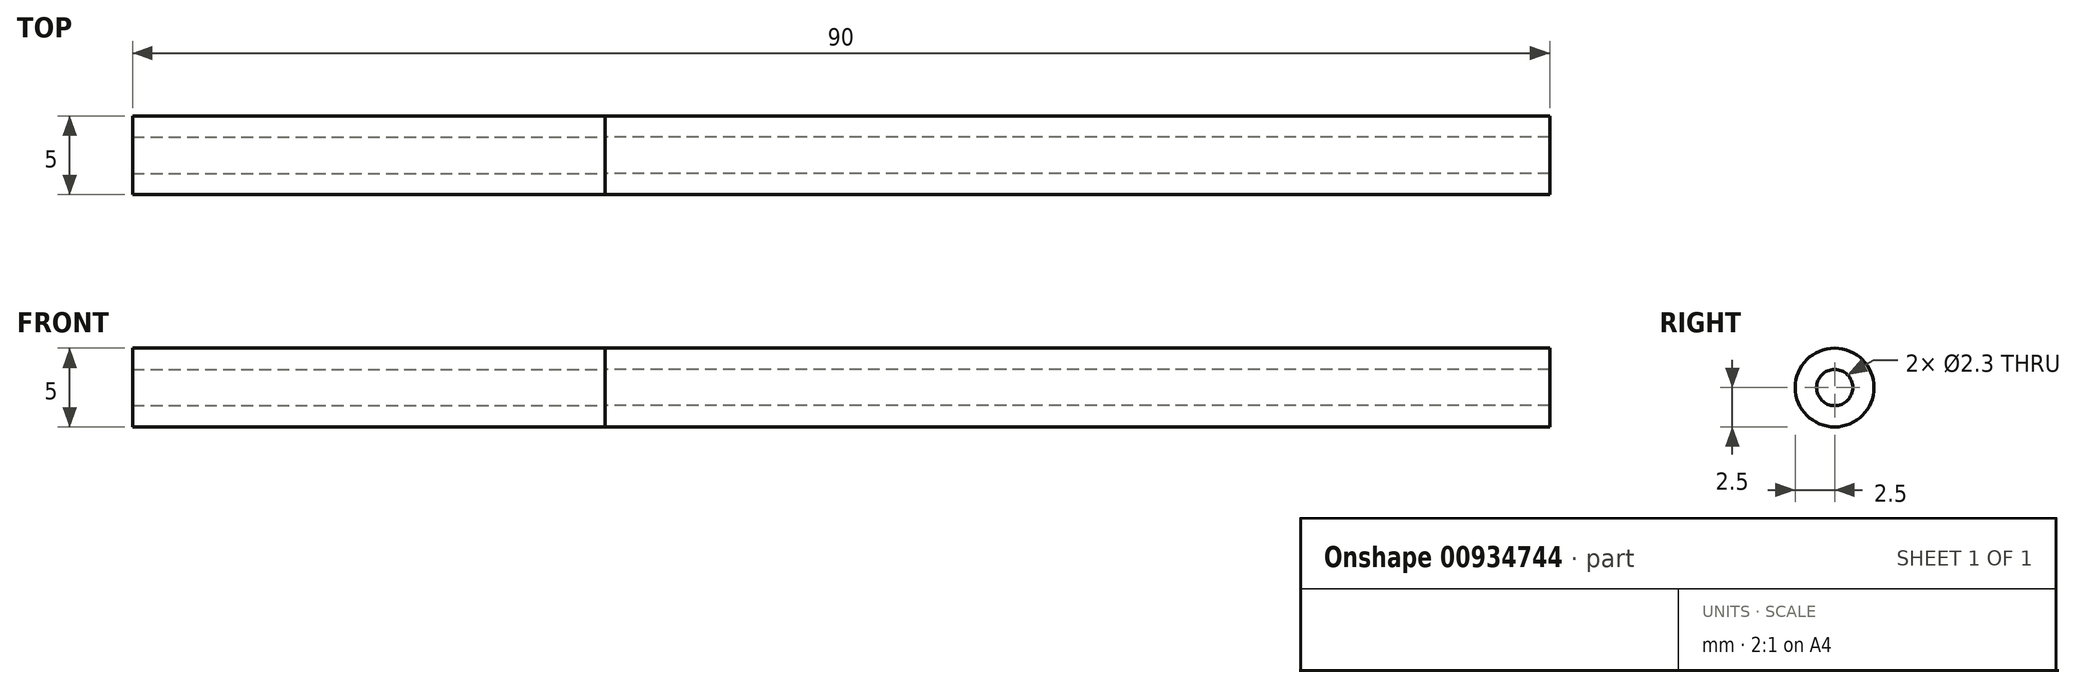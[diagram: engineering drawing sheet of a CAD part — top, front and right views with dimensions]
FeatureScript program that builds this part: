
annotation { "Feature Type Name" : "Feature", "Feature Type Description" : "" }
export const myFeature = defineFeature(function(context is Context, id is Id, definition is map)
    precondition{}
    {
        {
            var Q0;
            Q0=qCreatedBy(makeId("Right.planeOp"),FACE);
            var sketch = newSketch(context, id + "F0", { "sketchPlane" : qUnion([Q0])});
            skCircle(sketch, "E0", {"center": v(0, 0) * mm, "radius": 2.5 * mm});
            skCircle(sketch, "E1", {"center": v(0, 0) * mm, "radius": 1.15 * mm});
            skSolve(sketch);
        }
        {
            var Q0;
            Q0=makeQuery(id+"F0.imprint","IMPRINT",FACE,{"disambiguationData":[TD([[makeQuery(id+"F0.imprint","IMPRINT",EDGE,{"derivedFrom":sQuery(id+"F0.wireOp",EDGE,"E0")}),1.0]])]});
            extrude(context, id + "F1", {"entities" : qUnion([Q0]), "depth" : 60 * mm, "offsetDistance" : 25 * mm});
        }
        {
            var Q0;
            Q0=qCreatedBy(makeId("Right.planeOp"),FACE);
            var sketch = newSketch(context, id + "F2", { "sketchPlane" : qUnion([Q0])});
            skCircle(sketch, "E2", {"center": v(0, 0) * mm, "radius": 2.5 * mm});
            skCircle(sketch, "E3", {"center": v(0, 0) * mm, "radius": 1.15 * mm});
            skSolve(sketch);
        }
        {
            var Q0;
            Q0 = qSketchRegion(id + "F2", true);
            extrude(context, id + "F3", {"entities" : qUnion([Q0]), "oppositeDirection" : true, "depth" : 30 * mm, "offsetDistance" : 25 * mm});
        }
    });
